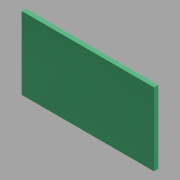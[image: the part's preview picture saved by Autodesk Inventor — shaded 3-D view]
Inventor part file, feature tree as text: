
AUTODESK INVENTOR PART (.ipt)
format: ipt  version: 2020 (Build 240168000, 168)  size: 76,288 bytes
history: native  units: mm
features: extrude x1, sketch x1
ambient origin geometry x8: Origin, YZ Plane, XZ Plane, XY Plane, X Axis, Y Axis, Z Axis, Center Point
bodies: Solid1 (feature_tree)
feature tree (2):
  extrude  "Extrusion1"  Depth=1.6mm TaperAngle=0.0deg
  sketch  "Sketch1"  dims[d0=51.0mm d1=1.6mm d2=0.0mm d3=27.8mm]
